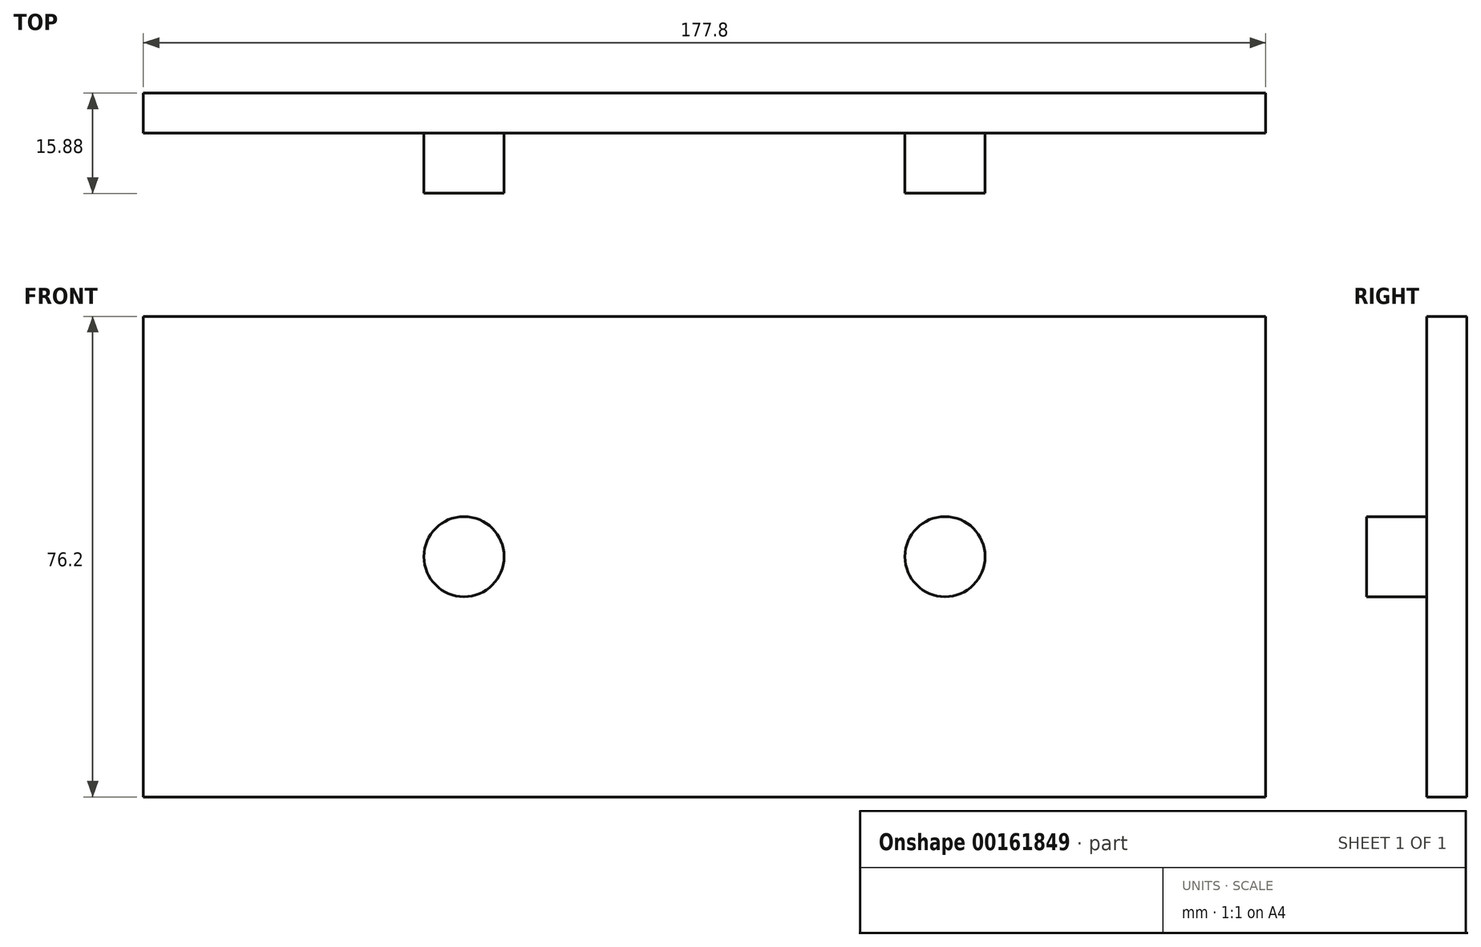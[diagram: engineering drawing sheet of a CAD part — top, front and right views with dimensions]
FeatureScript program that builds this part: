
annotation { "Feature Type Name" : "Feature", "Feature Type Description" : "" }
export const myFeature = defineFeature(function(context is Context, id is Id, definition is map)
    precondition{}
    {
        {
            var Q0;
            Q0=qCreatedBy(makeId("Front.planeOp"),FACE);
            var sketch = newSketch(context, id + "F0", { "sketchPlane" : qUnion([Q0])});
            skLineSegment(sketch, "E0.bottom", {"start": v(0, 0) * mm, "end": v(177.8, 0) * mm});
            skLineSegment(sketch, "E0.top", {"start": v(0, -76.2) * mm, "end": v(177.8, -76.2) * mm});
            skLineSegment(sketch, "E0.left", {"start": v(0, 0) * mm, "end": v(0, -76.2) * mm});
            skLineSegment(sketch, "E0.right", {"start": v(177.8, 0) * mm, "end": v(177.8, -76.2) * mm});
            skSolve(sketch);
        }
        {
            var Q0;
            Q0 = qSketchRegion(id + "F0", true);
            extrude(context, id + "F1", {"entities" : qUnion([Q0]), "depth" : 6.35 * mm});
        }
        {
            var Q0;
            Q0=makeQuery(id+"F1.opExtrude","CAP_FACE",FACE,{"disambiguationData":[OSD([sQuery(id+"F0.wireOp",EDGE,"E0.bottom"),sQuery(id+"F0.wireOp",EDGE,"E0.top"),sQuery(id+"F0.wireOp",EDGE,"E0.left"),sQuery(id+"F0.wireOp",EDGE,"E0.right")])],"isStart":false});
            var sketch = newSketch(context, id + "F2", { "sketchPlane" : qUnion([Q0])});
            skLineSegment(sketch, "E1", {"start": v(0, -38.1) * mm, "end": v(177.8, -38.1) * mm});
            skLineSegment(sketch, "E2", {"start": v(50.8, 0) * mm, "end": v(50.8, -76.2) * mm});
            skLineSegment(sketch, "E3", {"start": v(127, 0) * mm, "end": v(127, -76.2) * mm});
            skCircle(sketch, "E4", {"center": v(50.8, -38.1) * mm, "radius": 6.35 * mm});
            skCircle(sketch, "E5", {"center": v(127, -38.1) * mm, "radius": 6.35 * mm});
            skSolve(sketch);
        }
        {
            var Q0;
            Q0 = qSketchRegion(id + "F2", true);
            extrude(context, id + "F3", {"entities" : qUnion([Q0]), "operationType" : NewBodyOperationType.ADD, "depth" : 9.52 * mm});
        }
    });
